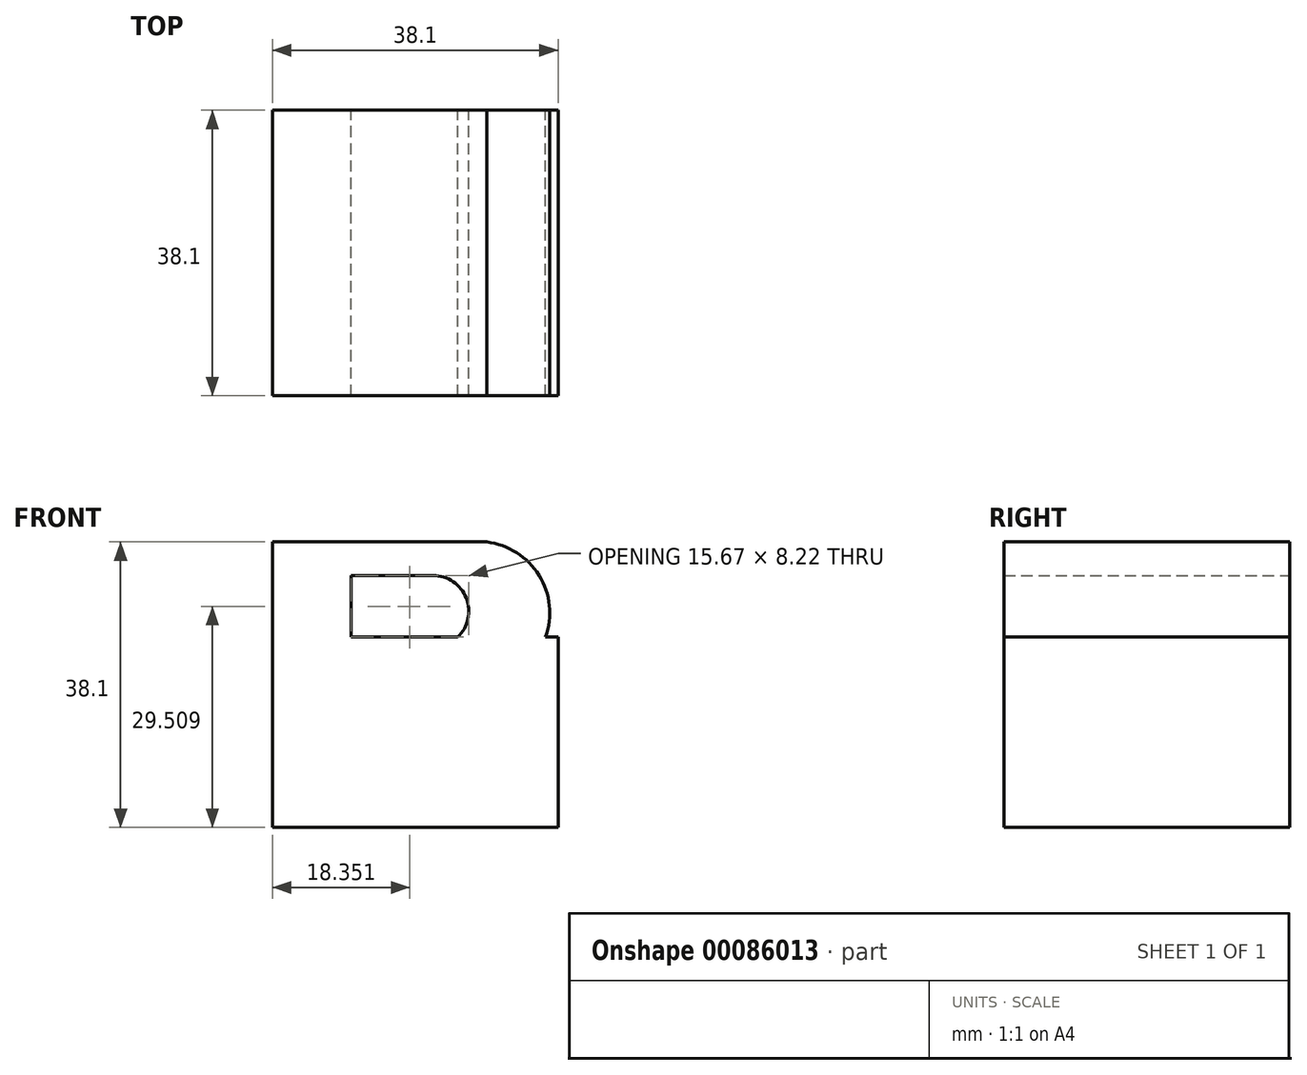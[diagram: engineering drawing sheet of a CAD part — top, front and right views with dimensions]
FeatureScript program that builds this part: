
annotation { "Feature Type Name" : "Feature", "Feature Type Description" : "" }
export const myFeature = defineFeature(function(context is Context, id is Id, definition is map)
    precondition{}
    {
        {
            var Q0;
            Q0=qCreatedBy(makeId("Front.planeOp"),FACE);
            var sketch = newSketch(context, id + "F0", { "sketchPlane" : qUnion([Q0])});
            skLineSegment(sketch, "E0", {"start": v(0, 0) * mm, "end": v(37.85, 0) * mm});
            skLineSegment(sketch, "E1", {"start": v(37.85, 0) * mm, "end": v(0, 0) * mm});
            skLineSegment(sketch, "E2", {"start": v(0, 0) * mm, "end": v(0, 38.1) * mm});
            skLineSegment(sketch, "E3", {"start": v(0, 38.1) * mm, "end": v(38.1, 38.1) * mm});
            skLineSegment(sketch, "E4", {"start": v(38.1, 38.1) * mm, "end": v(37.85, 0) * mm});
            skSolve(sketch);
        }
        {
            var Q0;
            Q0 = qSketchRegion(id + "F0", true);
            extrude(context, id + "F1", {"entities" : qUnion([Q0]), "depth" : 38.1 * mm});
        }
        {
            var Q0;
            Q0=qCreatedBy(makeId("Front.planeOp"),FACE);
            var sketch = newSketch(context, id + "F2", { "sketchPlane" : qUnion([Q0])});
            skLineSegment(sketch, "E5", {"start": v(0, 38.1) * mm, "end": v(0, 0) * mm});
            skLineSegment(sketch, "E6", {"start": v(0, 0) * mm, "end": v(0, 38.1) * mm});
            skLineSegment(sketch, "E7", {"start": v(10.51, 4.49) * mm, "end": v(10.51, 14.01) * mm});
            skLineSegment(sketch, "E8", {"start": v(10.51, 14.01) * mm, "end": v(21.44, 14.01) * mm});
            skLineSegment(sketch, "E9", {"start": v(10.51, 4.49) * mm, "end": v(21.44, 4.49) * mm});
            skLineSegment(sketch, "E10", {"start": v(10.51, 24.1) * mm, "end": v(10.51, 33.62) * mm});
            skLineSegment(sketch, "E11", {"start": v(10.51, 33.62) * mm, "end": v(21.44, 33.62) * mm});
            skLineSegment(sketch, "E12", {"start": v(0, 38.1) * mm, "end": v(19.05, 38.1) * mm});
            skLineSegment(sketch, "E13", {"start": v(0, 0) * mm, "end": v(19.05, 0) * mm});
            skLineSegment(sketch, "E14", {"start": v(10.51, 24.1) * mm, "end": v(21.44, 24.1) * mm});
            skArc(sketch, "E15", {"start": v(21.44, 33.62) * mm, "mid": v(26.2, 28.86) * mm, "end": v(21.44, 24.1) * mm});
            skLineSegment(sketch, "E16", {"start": v(0, 19.05) * mm, "end": v(19.05, 19.05) * mm});
            skLineSegment(sketch, "E17", {"start": v(19.05, 19.05) * mm, "end": v(27.44, 19.05) * mm});
            skLineSegment(sketch, "E18", {"start": v(19.05, 38.1) * mm, "end": v(28.57, 38.1) * mm});
            skLineSegment(sketch, "E19", {"start": v(19.05, 0) * mm, "end": v(28.58, 0) * mm});
            skArc(sketch, "E20", {"start": v(27.44, 19.05) * mm, "mid": v(36.98, 28.04) * mm, "end": v(28.57, 38.1) * mm});
            skArc(sketch, "E21", {"start": v(27.44, 19.05) * mm, "mid": v(36.98, 10.06) * mm, "end": v(28.58, 0) * mm});
            skLineSegment(sketch, "E22", {"start": v(38.1, 0) * mm, "end": v(38.1, 38.1) * mm});
            skLineSegment(sketch, "E23", {"start": v(38.1, 38.1) * mm, "end": v(28.57, 38.1) * mm});
            skLineSegment(sketch, "E24", {"start": v(38.1, 0) * mm, "end": v(0, 0) * mm});
            skArc(sketch, "E25", {"start": v(21.44, 14.01) * mm, "mid": v(26.2, 9.25) * mm, "end": v(21.44, 4.49) * mm});
            skSolve(sketch);
        }
        {
            var Q0;
            Q0=makeQuery(id+"F2.imprint","IMPRINT",FACE,{"disambiguationData":[TD([[makeQuery(id+"F2.imprint","IMPRINT",EDGE,{"derivedFrom":sQuery(id+"F2.wireOp",EDGE,"E10")}),-1.0]])]});
            var Q1;
            Q1=makeQuery(id+"F2.imprint","IMPRINT",FACE,{"disambiguationData":[TD([[makeQuery(id+"F2.imprint","IMPRINT",EDGE,{"derivedFrom":sQuery(id+"F2.wireOp",EDGE,"E7")}),-1.0]])]});
            var Q2;
            Q2=makeQuery(id+"F2.imprint","IMPRINT",FACE,{"disambiguationData":[TD([[makeQuery(id+"F2.imprint","IMPRINT",EDGE,{"derivedFrom":sQuery(id+"F2.wireOp",EDGE,"E20")}),-1.0]])]});
            extrude(context, id + "F3", {"entities" : qUnion([Q0, Q1, Q2]), "operationType" : NewBodyOperationType.REMOVE, "depth" : 38.1 * mm});
        }
        {
            var Q0;
            Q0=qCreatedBy(makeId("Top.planeOp"),FACE);
            var sketch = newSketch(context, id + "F4", { "sketchPlane" : qUnion([Q0])});
            skLineSegment(sketch, "E26", {"start": v(0, 0) * mm, "end": v(0, -38.1) * mm});
            skLineSegment(sketch, "E27", {"start": v(0, -38.1) * mm, "end": v(38.1, -38.1) * mm});
            skLineSegment(sketch, "E28", {"start": v(38.1, -38.1) * mm, "end": v(38.1, 0) * mm});
            skLineSegment(sketch, "E29", {"start": v(38.1, 0) * mm, "end": v(0, 0) * mm});
            skLineSegment(sketch, "E30", {"start": v(38.1, -7.62) * mm, "end": v(7.62, -7.62) * mm});
            skLineSegment(sketch, "E31", {"start": v(7.62, -7.62) * mm, "end": v(7.62, -30.48) * mm});
            skLineSegment(sketch, "E32", {"start": v(7.62, -30.48) * mm, "end": v(38.1, -30.48) * mm});
            skLineSegment(sketch, "E33", {"start": v(7.62, -9.45) * mm, "end": v(7.62, -30.48) * mm});
            skLineSegment(sketch, "E34", {"start": v(7.62, -7.62) * mm, "end": v(38.1, -7.62) * mm});
            skLineSegment(sketch, "E35", {"start": v(7.62, -30.48) * mm, "end": v(7.62, -7.62) * mm});
            skSolve(sketch);
        }
        {
            var Q0;
            Q0 = qSketchRegion(id + "F4", true);
            extrude(context, id + "F5", {"entities" : qUnion([Q0]), "operationType" : NewBodyOperationType.ADD, "depth" : 25.4 * mm});
        }
        {
            var Q0;
            Q0 = qSketchRegion(id + "F4", true);
            extrude(context, id + "F6", {"entities" : qUnion([Q0]), "operationType" : NewBodyOperationType.ADD, "depth" : 25.4 * mm});
        }
    });
